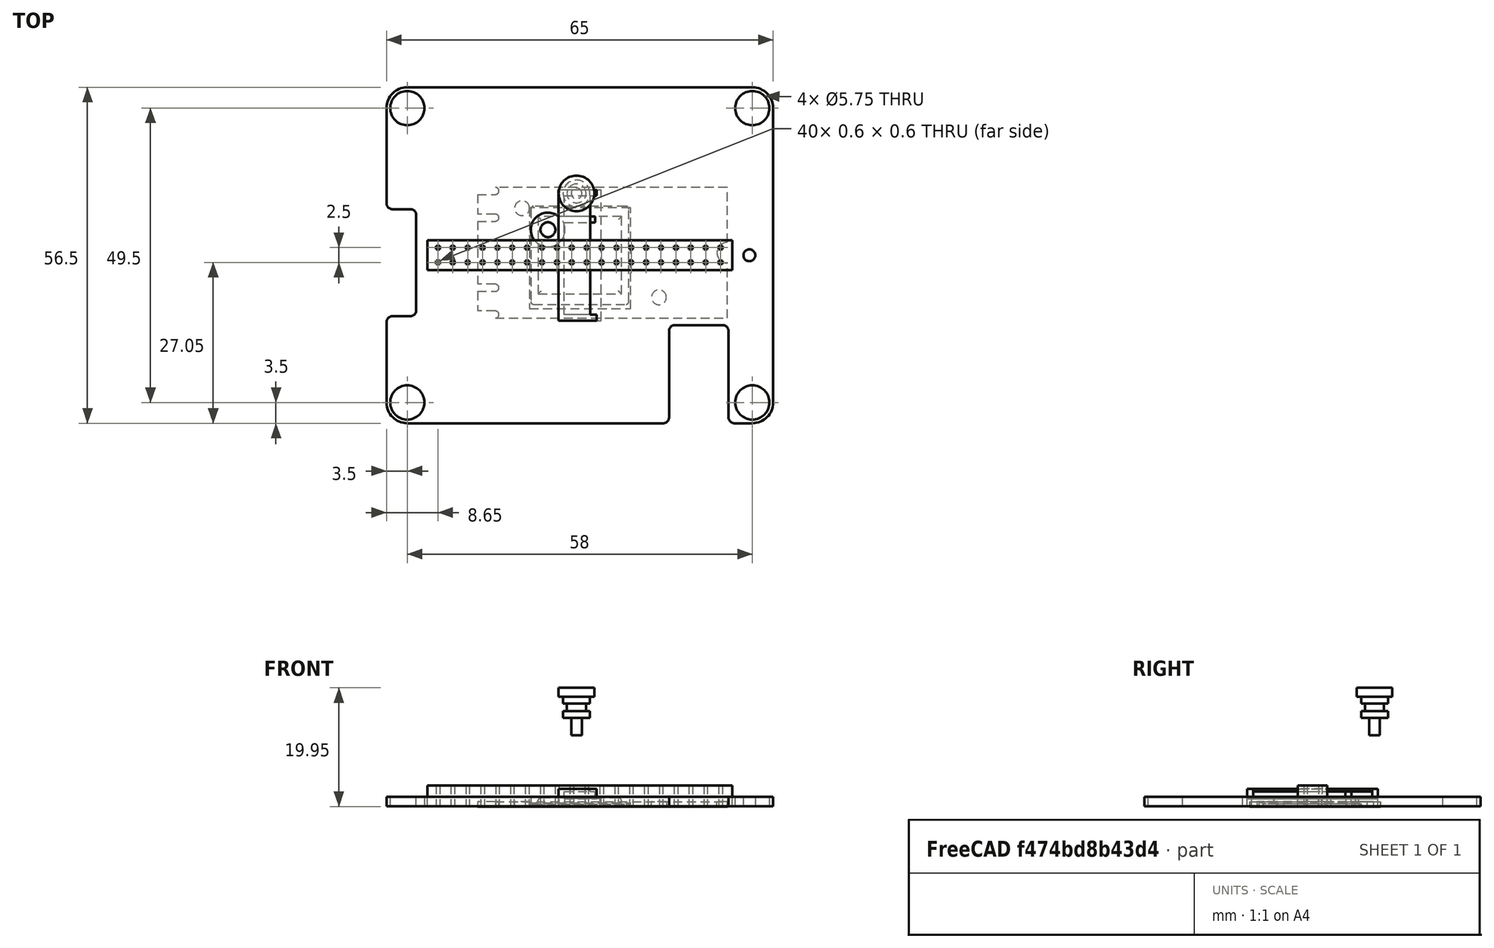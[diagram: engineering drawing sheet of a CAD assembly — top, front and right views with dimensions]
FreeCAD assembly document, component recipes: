
FREECAD ASSEMBLY — COMPONENT RECIPES ("Raspberry Pi AI Kit")

This assembly document has 11 components, labeled P0..P10 below (a component is one placed body or linked part). 11 of them carry a construction recipe — the FreeCAD feature program that regenerates the part from scratch, quoted from this document or its linked companion documents; the rest are supplied as boundary geometry only. No exploded tour is included for this assembly.
COMPONENT P0 — recipe-attached ("Board001", modeled in this document).
Construction recipe (the document's own serialized feature program — sketch geometry with constraints, then the solid features built on it; lengths are millimeters unless a unit is written):

FEATURE [Sketcher::SketchObject] Sketch
  ArcFitTolerance = 1e-06
  AttachmentSupport = -> [XY_Plane003]
  FullyConstrained = true
  MakeInternals = false
  MapMode = 5
  sketch-geometry (6):
    g0: LineSegment StartX=-21 StartY=11 StartZ=0 EndX=-21 EndY=-11 EndZ=0
    g1: LineSegment StartX=-21 StartY=-11 StartZ=0 EndX=21 EndY=-11 EndZ=0
    g2: LineSegment StartX=21 StartY=-11 StartZ=0 EndX=21 EndY=11 EndZ=0
    g3: LineSegment StartX=21 StartY=11 StartZ=0 EndX=-21 EndY=11 EndZ=0
    g4: GeomPoint X=0 Y=11 Z=0
    g5: GeomPoint X=-21 Y=0 Z=0
  constraints (14):
    c: Coincident(g0,g1)
    c: Coincident(g1,g2)
    c: Coincident(g2,g3)
    c: Coincident(g3,g0)
    c: Vertical(g0)
    c: Vertical(g2)
    c: Horizontal(g1)
    c: Horizontal(g3)
    c: DistanceY(g2,g2) = 22
    c: DistanceX(g3,g3) = 42
    c: Symmetric(g3,g3,g4)
    c: Symmetric(g0,g0,g5)
    c: Vertical(g4,g-1)
    c: Horizontal(g5,g-1)
FEATURE [PartDesign::Pad] Pad
  Direction = (0,0,1)
  Length = 0.8
  Length2 = 10
  Profile = -> Sketch
  ReferenceAxis = -> Sketch [N_Axis]
  Refine = true
  Suppressed = false
  Type = 0
FEATURE [Sketcher::SketchObject] Sketch001
  ArcFitTolerance = 1e-06
  AttachmentSupport = -> [Pad]
  ExternalGeometry = -> [Pad]
  FullyConstrained = true
  MakeInternals = false
  MapMode = 5
  Placement = pos=(0,0,0.8) rot=(0,0,1;0rad)
  sketch-geometry (27):
    g0: LineSegment StartX=-21 StartY=-9.8 StartZ=0 EndX=-21 EndY=-11 EndZ=0
    g1: LineSegment StartX=-21 StartY=-11 StartZ=0 EndX=-18 EndY=-11 EndZ=0
    g2: LineSegment StartX=-18 StartY=-11 StartZ=0 EndX=-18 EndY=-9.8 EndZ=0
    g3: LineSegment StartX=-18 StartY=-9.8 StartZ=0 EndX=-21 EndY=-9.8 EndZ=0
    g4: GeomPoint X=-18 Y=-10.4 Z=0
    g5: Circle CenterX=-18 CenterY=-10.4 CenterZ=0 NormalX=0 NormalY=0 NormalZ=1 AngleXU=0 Radius=0.6
    g6: Circle CenterX=21 CenterY=0 CenterZ=0 NormalX=0 NormalY=0 NormalZ=1 AngleXU=0 Radius=1.75
    g7: LineSegment StartX=-21 StartY=11 StartZ=0 EndX=-21 EndY=9.8 EndZ=0
    g8: LineSegment StartX=-21 StartY=9.8 StartZ=0 EndX=-18 EndY=9.8 EndZ=0
    g9: LineSegment StartX=-18 StartY=9.8 StartZ=0 EndX=-18 EndY=11 EndZ=0
    g10: LineSegment StartX=-18 StartY=11 StartZ=0 EndX=-21 EndY=11 EndZ=0
    g11: GeomPoint X=-18 Y=10.4 Z=0
    g12: Circle CenterX=-18 CenterY=10.4 CenterZ=0 NormalX=0 NormalY=0 NormalZ=1 AngleXU=0 Radius=0.6
    g13: LineSegment StartX=-21 StartY=6.5 StartZ=0 EndX=-21 EndY=5.3 EndZ=0
    g14: LineSegment StartX=-21 StartY=5.3 StartZ=0 EndX=-18 EndY=5.3 EndZ=0
    g15: LineSegment StartX=-18 StartY=5.3 StartZ=0 EndX=-18 EndY=6.5 EndZ=0
    g16: LineSegment StartX=-18 StartY=6.5 StartZ=0 EndX=-21 EndY=6.5 EndZ=0
    g17: GeomPoint X=-18 Y=5.9 Z=0
    g18: Circle CenterX=-18 CenterY=5.9 CenterZ=0 NormalX=0 NormalY=0 NormalZ=1 AngleXU=0 Radius=0.6
    g19: LineSegment StartX=-21 StartY=-5.3 StartZ=0 EndX=-21 EndY=-6.5 EndZ=0
    g20: LineSegment StartX=-21 StartY=-6.5 StartZ=0 EndX=-18 EndY=-6.5 EndZ=0
    g21: LineSegment StartX=-18 StartY=-6.5 StartZ=0 EndX=-18 EndY=-5.3 EndZ=0
    g22: LineSegment StartX=-18 StartY=-5.3 StartZ=0 EndX=-21 EndY=-5.3 EndZ=0
    g23: GeomPoint X=-18 Y=-5.9 Z=0
    g24: Circle CenterX=-18 CenterY=-5.9 CenterZ=0 NormalX=0 NormalY=0 NormalZ=1 AngleXU=0 Radius=0.6
    g25: Circle CenterX=-13.5 CenterY=7.5 CenterZ=0 NormalX=0 NormalY=0 NormalZ=1 AngleXU=0 Radius=1.25
    g26: Circle CenterX=9.5 CenterY=-7.5 CenterZ=0 NormalX=0 NormalY=0 NormalZ=1 AngleXU=0 Radius=1.25
  constraints (66):
    c: Coincident(g0,g1)
    c: Coincident(g1,g2)
    c: Coincident(g2,g3)
    c: Coincident(g3,g0)
    c: Vertical(g0)
    c: Vertical(g2)
    c: Horizontal(g1)
    c: Horizontal(g3)
    c: Symmetric(g2,g2,g4)
    c: Coincident(g5,g4)
    c: PointOnObject(g2,g5)
    c: Distance(g1,g3) = 1.2
    c: DistanceX(g3,g3) = 3
    c: Symmetric(g-6,g-6,g6)
    c: Diameter(g6) = 3.5
    c: Coincident(g7,g8)
    c: Coincident(g8,g9)
    c: Coincident(g9,g10)
    c: Coincident(g10,g7)
    c: Vertical(g7)
    c: Vertical(g9)
    c: Horizontal(g8)
    c: Horizontal(g10)
    c: Symmetric(g9,g9,g11)
    c: Coincident(g12,g11)
    c: PointOnObject(g9,g12)
    c: Distance(g8,g10) = 1.2
    c: DistanceX(g10,g10) = 3
    c: Coincident(g0,g-5)
    c: Coincident(g13,g14)
    c: Coincident(g14,g15)
    c: Coincident(g15,g16)
    c: Coincident(g16,g13)
    c: Vertical(g13)
    c: Vertical(g15)
    c: Horizontal(g14)
    c: Horizontal(g16)
    c: Symmetric(g15,g15,g17)
    c: Coincident(g18,g17)
    c: PointOnObject(g15,g18)
    c: Distance(g14,g16) = 1.2
    c: DistanceX(g16,g16) = 3
    c: Coincident(g19,g20)
    c: Coincident(g20,g21)
    c: Coincident(g21,g22)
    c: Coincident(g22,g19)
    c: Vertical(g19)
    c: Vertical(g21)
    c: Horizontal(g20)
    c: Horizontal(g22)
    c: Symmetric(g21,g21,g23)
    c: Coincident(g24,g23)
    c: PointOnObject(g21,g24)
    c: Distance(g20,g22) = 1.2
    c: DistanceX(g22,g22) = 3
    c: Coincident(g7,g-4)
    c: Distance(g-4,g16) = 4.5
    c: PointOnObject(g13,g-3)
    c: Distance(g-5,g20) = 4.5
    c: PointOnObject(g19,g-3)
    c: Diameter(g25) = 2.5
    c: Diameter(g26) = 2.5
    c: Distance(g25,g-5) = 18.5
    c: Distance(g25,g-3) = 7.5
    c: Distance(g26,g-5) = 3.5
    c: Distance(g26,g-3) = 30.5
FEATURE [PartDesign::Pocket] Pocket
  BaseFeature = -> Pad
  Direction = (0,0,-1)
  Length = 5
  Length2 = 5
  Profile = -> Sketch001
  ReferenceAxis = -> Sketch001 [N_Axis]
  Refine = true
  Suppressed = false
  Type = 0
FEATURE [PartDesign::Body] Body  label="Board"
  AllowCompound = false
  Group = -> [Sketch,Pad,Sketch001,Pocket]
  Origin = -> Origin003
  Placement = pos=(3.79899,0.428775,-0.0438795) rot=(0,0,1;0rad)
  Tip = -> Pocket
COMPONENT P1 — recipe-attached ("Board003", modeled in this document).
Construction recipe (the document's own serialized feature program — sketch geometry with constraints, then the solid features built on it; lengths are millimeters unless a unit is written):

FEATURE [Sketcher::SketchObject] Sketch006
  ArcFitTolerance = 1e-06
  AttachmentSupport = -> [XY_Plane010]
  FullyConstrained = true
  MakeInternals = false
  MapMode = 5
  sketch-geometry (38):
    g0: LineSegment StartX=-29 StartY=28.25 StartZ=0 EndX=29 EndY=28.25 EndZ=0
    g1: LineSegment StartX=32.5 StartY=24.75 StartZ=0 EndX=32.5 EndY=-24.75 EndZ=0
    g2: LineSegment StartX=29 StartY=-28.25 StartZ=0 EndX=26 EndY=-28.25 EndZ=0
    g3: LineSegment StartX=25 StartY=-27.25 StartZ=0 EndX=25 EndY=-12.75 EndZ=0
    g4: LineSegment StartX=24 StartY=-11.75 StartZ=0 EndX=16 EndY=-11.75 EndZ=0
    g5: LineSegment StartX=15 StartY=-12.75 StartZ=0 EndX=15 EndY=-27.25 EndZ=0
    g6: LineSegment StartX=14 StartY=-28.25 StartZ=0 EndX=-29 EndY=-28.25 EndZ=0
    g7: GeomPoint X=0 Y=28.25 Z=0
    g8: LineSegment StartX=-32.5 StartY=-24.75 StartZ=0 EndX=-32.5 EndY=-11.25 EndZ=0
    g9: LineSegment StartX=-31.5 StartY=-10.25 StartZ=0 EndX=-28.5 EndY=-10.25 EndZ=0
    g10: LineSegment StartX=-27.5 StartY=-9.25 StartZ=0 EndX=-27.5 EndY=6.75 EndZ=0
    g11: LineSegment StartX=-28.5 StartY=7.75 StartZ=0 EndX=-31.5 EndY=7.75 EndZ=0
    g12: LineSegment StartX=-32.5 StartY=8.75 StartZ=0 EndX=-32.5 EndY=24.75 EndZ=0
    g13: GeomPoint X=32.5 Y=0 Z=0
    g14: ArcOfCircle CenterX=29 CenterY=24.75 CenterZ=0 NormalX=0 NormalY=0 NormalZ=1 AngleXU=0 Radius=3.5 StartAngle=0 EndAngle=1.5708
    g15: GeomPoint [constr] X=32.5 Y=28.25 Z=0
    g16: ArcOfCircle CenterX=-29 CenterY=24.75 CenterZ=0 NormalX=0 NormalY=0 NormalZ=1 AngleXU=0 Radius=3.5 StartAngle=1.5708 EndAngle=3.14159
    g17: GeomPoint [constr] X=-32.5 Y=28.25 Z=0
    g18: ArcOfCircle CenterX=-29 CenterY=-24.75 CenterZ=0 NormalX=0 NormalY=0 NormalZ=1 AngleXU=0 Radius=3.5 StartAngle=3.14159 EndAngle=4.71239
    g19: GeomPoint [constr] X=-32.5 Y=-28.25 Z=0
    g20: ArcOfCircle CenterX=29 CenterY=-24.75 CenterZ=0 NormalX=0 NormalY=0 NormalZ=1 AngleXU=0 Radius=3.5 StartAngle=4.71239 EndAngle=6.28319
    g21: GeomPoint [constr] X=32.5 Y=-28.25 Z=0
    g22: ArcOfCircle CenterX=-31.5 CenterY=8.75 CenterZ=0 NormalX=0 NormalY=0 NormalZ=1 AngleXU=0 Radius=1 StartAngle=3.14159 EndAngle=4.71239
    g23: GeomPoint [constr] X=-32.5 Y=7.75 Z=0
    g24: ArcOfCircle CenterX=-28.5 CenterY=6.75 CenterZ=0 NormalX=0 NormalY=0 NormalZ=1 AngleXU=0 Radius=1 StartAngle=0 EndAngle=1.5708
    g25: GeomPoint [constr] X=-27.5 Y=7.75 Z=0
    g26: ArcOfCircle CenterX=-28.5 CenterY=-9.25 CenterZ=0 NormalX=0 NormalY=0 NormalZ=1 AngleXU=0 Radius=1 StartAngle=4.71239 EndAngle=6.28319
    g27: GeomPoint [constr] X=-27.5 Y=-10.25 Z=0
    g28: ArcOfCircle CenterX=-31.5 CenterY=-11.25 CenterZ=0 NormalX=0 NormalY=0 NormalZ=1 AngleXU=0 Radius=1 StartAngle=1.5708 EndAngle=3.14159
    g29: GeomPoint [constr] X=-32.5 Y=-10.25 Z=0
    g30: ArcOfCircle CenterX=14 CenterY=-27.25 CenterZ=0 NormalX=0 NormalY=0 NormalZ=1 AngleXU=0 Radius=1 StartAngle=4.71239 EndAngle=6.28319
    g31: GeomPoint [constr] X=15 Y=-28.25 Z=0
    g32: ArcOfCircle CenterX=16 CenterY=-12.75 CenterZ=0 NormalX=0 NormalY=0 NormalZ=1 AngleXU=0 Radius=1 StartAngle=1.5708 EndAngle=3.14159
    g33: GeomPoint [constr] X=15 Y=-11.75 Z=0
    g34: ArcOfCircle CenterX=24 CenterY=-12.75 CenterZ=0 NormalX=0 NormalY=0 NormalZ=1 AngleXU=0 Radius=1 StartAngle=4e-16 EndAngle=1.5708
    g35: GeomPoint [constr] X=25 Y=-11.75 Z=0
    g36: ArcOfCircle CenterX=26 CenterY=-27.25 CenterZ=0 NormalX=0 NormalY=0 NormalZ=1 AngleXU=0 Radius=1 StartAngle=3.14159 EndAngle=4.71239
    g37: GeomPoint [constr] X=25 Y=-28.25 Z=0
  constraints (86):
    c: Horizontal(g0)
    c: Vertical(g1)
    c: Horizontal(g2)
    c: Vertical(g3)
    c: Horizontal(g4)
    c: Vertical(g5)
    c: Horizontal(g6)
    c: DistanceX(g17,g15) = 65
    c: Symmetric(g17,g15,g7)
    c: Vertical(g7,g-1)
    c: Horizontal(g37,g31)
    c: DistanceX(g37,g21) = 7.5
    c: DistanceX(g33,g35) = 10
    c: DistanceY(g37,g35) = 16.5
    c: Vertical(g8)
    c: Horizontal(g9)
    c: Vertical(g10)
    c: Horizontal(g11)
    c: Vertical(g12)
    c: Vertical(g23,g29)
    c: Symmetric(g15,g21,g13)
    c: Horizontal(g13,g-1)
    c: DistanceY(g21,g15) = 56.5
    c: DistanceX(g23,g25) = 5
    c: DistanceY(g27,g25) = 18
    c: DistanceY(g19,g29) = 18
    c: PointOnObject(g15,g0)
    c: PointOnObject(g15,g1)
    c: Tangent(g0,g14) = 1.5708
    c: Tangent(g1,g14) = 1.5708
    c: PointOnObject(g17,g0)
    c: PointOnObject(g17,g12)
    c: Tangent(g0,g16) = 1.5708
    c: Tangent(g12,g16) = 1.5708
    c: PointOnObject(g19,g6)
    c: PointOnObject(g19,g8)
    c: Tangent(g6,g18) = 1.5708
    c: Tangent(g8,g18) = 1.5708
    c: PointOnObject(g21,g1)
    c: PointOnObject(g21,g2)
    c: Tangent(g1,g20) = 1.5708
    c: Tangent(g2,g20) = 1.5708
    c: Radius(g20) = 3.5
    c: Radius(g14) = 3.5
    c: Radius(g16) = 3.5
    c: Radius(g18) = 3.5
    c: PointOnObject(g23,g11)
    c: PointOnObject(g23,g12)
    c: Tangent(g11,g22) = 1.5708
    c: Tangent(g12,g22) = 1.5708
    c: PointOnObject(g25,g10)
    c: PointOnObject(g25,g11)
    c: Tangent(g10,g24) = -1.5708
    c: Tangent(g11,g24) = -1.5708
    c: PointOnObject(g27,g9)
    c: PointOnObject(g27,g10)
    c: Tangent(g9,g26) = -1.5708
    c: Tangent(g10,g26) = -1.5708
    c: PointOnObject(g29,g8)
    c: PointOnObject(g29,g9)
    c: Tangent(g8,g28) = 1.5708
    c: Tangent(g9,g28) = 1.5708
    c: PointOnObject(g31,g5)
    c: PointOnObject(g31,g6)
    c: Tangent(g5,g30) = 1.5708
    c: Tangent(g6,g30) = 1.5708
    c: PointOnObject(g33,g4)
    c: PointOnObject(g33,g5)
    c: Tangent(g4,g32) = -1.5708
    c: Tangent(g5,g32) = -1.5708
    c: PointOnObject(g35,g3)
    c: PointOnObject(g35,g4)
    c: Tangent(g3,g34) = -1.5708
    c: Tangent(g4,g34) = -1.5708
    c: PointOnObject(g37,g2)
    c: PointOnObject(g37,g3)
    c: Tangent(g2,g36) = 1.5708
    c: Tangent(g3,g36) = 1.5708
    c: Radius(g22) = 1
    c: Radius(g24) = 1
    c: Radius(g26) = 1
    c: Radius(g28) = 1
    c: Radius(g30) = 1
    c: Radius(g32) = 1
    c: Radius(g34) = 1
    c: Radius(g36) = 1
FEATURE [PartDesign::Pad] Pad004
  Direction = (0,0,1)
  Length = 1.57
  Length2 = 10
  Profile = -> Sketch006
  ReferenceAxis = -> Sketch006 [N_Axis]
  Refine = true
  Suppressed = false
  Type = 0
FEATURE [Sketcher::SketchObject] Sketch007
  ArcFitTolerance = 1e-06
  AttachmentSupport = -> [Pad004]
  ExternalGeometry = -> [Pad004]
  FullyConstrained = true
  MakeInternals = false
  MapMode = 5
  Placement = pos=(0,0,1.57) rot=(0,0,1;0rad)
  sketch-geometry (5):
    g0: Circle CenterX=-29 CenterY=-24.75 CenterZ=0 NormalX=0 NormalY=0 NormalZ=1 AngleXU=0 Radius=2.875
    g1: Circle CenterX=-29 CenterY=24.75 CenterZ=0 NormalX=0 NormalY=0 NormalZ=1 AngleXU=0 Radius=2.875
    g2: Circle CenterX=29 CenterY=24.75 CenterZ=0 NormalX=0 NormalY=0 NormalZ=1 AngleXU=0 Radius=2.875
    g3: Circle CenterX=29 CenterY=-24.75 CenterZ=0 NormalX=0 NormalY=0 NormalZ=1 AngleXU=0 Radius=2.875
    g4: Circle CenterX=28.5 CenterY=0 CenterZ=0 NormalX=0 NormalY=0 NormalZ=1 AngleXU=0 Radius=1
  constraints (15):
    c: Distance(g0,g-3) = 3.5
    c: Distance(g0,g-7) = 3.5
    c: Diameter(g0) = 5.75
    c: Diameter(g1) = 5.75
    c: Diameter(g2) = 5.75
    c: Diameter(g3) = 5.75
    c: Distance(g1,g-6) = 3.5
    c: Distance(g1,g-5) = 3.5
    c: Distance(g2,g-5) = 3.5
    c: Distance(g2,g-4) = 3.5
    c: Distance(g3,g-4) = 3.5
    c: Distance(g3,g-3) = 3.5
    c: PointOnObject(g4,g-1)
    c: Diameter(g4) = 2
    c: Distance(g4,g-4) = 4
FEATURE [PartDesign::Pocket] Pocket001
  BaseFeature = -> Pad004
  Direction = (0,0,-1)
  Length = 5
  Length2 = 5
  Profile = -> Sketch007
  ReferenceAxis = -> Sketch007 [N_Axis]
  Refine = true
  Suppressed = false
  Type = 0
FEATURE [PartDesign::Body] Body004  label="Board002"
  AllowCompound = false
  Group = -> [Sketch006,Pad004,Sketch007,Pocket001]
  Origin = -> Origin010
  Tip = -> Pocket001
COMPONENT P2 — recipe-attached ("Chip001", modeled in this document).
Construction recipe (the document's own serialized feature program — sketch geometry with constraints, then the solid features built on it; lengths are millimeters unless a unit is written):

FEATURE [Sketcher::SketchObject] Sketch004
  ArcFitTolerance = 1e-06
  AttachmentSupport = -> [XY_Plane008]
  FullyConstrained = true
  MakeInternals = false
  MapMode = 5
  sketch-geometry (14):
    g0: LineSegment StartX=-8.25 StartY=7.75 StartZ=0 EndX=-8.25 EndY=-7.75 EndZ=0
    g1: LineSegment StartX=-7.75 StartY=-8.25 StartZ=0 EndX=7.75 EndY=-8.25 EndZ=0
    g2: LineSegment StartX=8.25 StartY=-7.75 StartZ=0 EndX=8.25 EndY=7.75 EndZ=0
    g3: LineSegment StartX=7.75 StartY=8.25 StartZ=0 EndX=-7.75 EndY=8.25 EndZ=0
    g4: GeomPoint X=8.25 Y=0 Z=0
    g5: GeomPoint X=0 Y=8.25 Z=0
    g6: ArcOfCircle CenterX=7.75 CenterY=7.75 CenterZ=0 NormalX=0 NormalY=0 NormalZ=1 AngleXU=0 Radius=0.5 StartAngle=2e-16 EndAngle=1.5708
    g7: GeomPoint [constr] X=8.25 Y=8.25 Z=0
    g8: ArcOfCircle CenterX=-7.75 CenterY=7.75 CenterZ=0 NormalX=0 NormalY=0 NormalZ=1 AngleXU=0 Radius=0.5 StartAngle=1.5708 EndAngle=3.14159
    g9: GeomPoint [constr] X=-8.25 Y=8.25 Z=0
    g10: ArcOfCircle CenterX=-7.75 CenterY=-7.75 CenterZ=0 NormalX=0 NormalY=0 NormalZ=1 AngleXU=0 Radius=0.5 StartAngle=3.14159 EndAngle=4.71239
    g11: GeomPoint [constr] X=-8.25 Y=-8.25 Z=0
    g12: ArcOfCircle CenterX=7.75 CenterY=-7.75 CenterZ=0 NormalX=0 NormalY=0 NormalZ=1 AngleXU=0 Radius=0.5 StartAngle=4.71239 EndAngle=6.28319
    g13: GeomPoint [constr] X=8.25 Y=-8.25 Z=0
  constraints (30):
    c: Vertical(g0)
    c: Vertical(g2)
    c: Horizontal(g1)
    c: Horizontal(g3)
    c: DistanceX(g9,g7) = 16.5
    c: DistanceY(g13,g7) = 16.5
    c: Symmetric(g13,g7,g4)
    c: Symmetric(g7,g9,g5)
    c: Vertical(g5,g-1)
    c: Horizontal(g4,g-1)
    c: PointOnObject(g7,g2)
    c: PointOnObject(g7,g3)
    c: Tangent(g2,g6) = -1.5708
    c: Tangent(g3,g6) = -1.5708
    c: PointOnObject(g9,g0)
    c: PointOnObject(g9,g3)
    c: Tangent(g0,g8) = -1.5708
    c: Tangent(g3,g8) = -1.5708
    c: PointOnObject(g11,g0)
    c: PointOnObject(g11,g1)
    c: Tangent(g0,g10) = -1.5708
    c: Tangent(g1,g10) = -1.5708
    c: PointOnObject(g13,g1)
    c: PointOnObject(g13,g2)
    c: Tangent(g1,g12) = -1.5708
    c: Tangent(g2,g12) = -1.5708
    c: Radius(g8) = 0.5
    c: Radius(g6) = 0.5
    c: Radius(g12) = 0.5
    c: Radius(g10) = 0.5
FEATURE [PartDesign::Pad] Pad002
  Direction = (0,0,1)
  Length = 0.4
  Length2 = 10
  Profile = -> Sketch004
  ReferenceAxis = -> Sketch004 [N_Axis]
  Refine = true
  Suppressed = false
  Type = 0
FEATURE [Sketcher::SketchObject] Sketch005
  ArcFitTolerance = 1e-06
  AttachmentSupport = -> [Pad002]
  FullyConstrained = true
  MakeInternals = false
  MapMode = 5
  Placement = pos=(0,0,0.4) rot=(0,0,1;0rad)
  sketch-geometry (6):
    g0: LineSegment StartX=-7 StartY=6.5 StartZ=0 EndX=-7 EndY=-6.5 EndZ=0
    g1: LineSegment StartX=-7 StartY=-6.5 StartZ=0 EndX=7 EndY=-6.5 EndZ=0
    g2: LineSegment StartX=7 StartY=-6.5 StartZ=0 EndX=7 EndY=6.5 EndZ=0
    g3: LineSegment StartX=7 StartY=6.5 StartZ=0 EndX=-7 EndY=6.5 EndZ=0
    g4: GeomPoint X=0 Y=6.5 Z=0
    g5: GeomPoint X=7 Y=-1e-16 Z=0
  constraints (14):
    c: Coincident(g0,g1)
    c: Coincident(g1,g2)
    c: Coincident(g2,g3)
    c: Coincident(g3,g0)
    c: Vertical(g0)
    c: Vertical(g2)
    c: Horizontal(g1)
    c: Horizontal(g3)
    c: Symmetric(g3,g3,g4)
    c: Symmetric(g2,g2,g5)
    c: Vertical(g4,g-1)
    c: Horizontal(g5,g-1)
    c: DistanceX(g3,g3) = 14
    c: DistanceY(g2,g2) = 13
FEATURE [PartDesign::Pad] Pad003
  BaseFeature = -> Pad002
  Direction = (0,0,1)
  Length = 1
  Length2 = 10
  Profile = -> Sketch005
  ReferenceAxis = -> Sketch005 [N_Axis]
  Refine = true
  Suppressed = false
  Type = 0
FEATURE [PartDesign::Fillet] Fillet
  Base = -> Pad003 [Face15]
  BaseFeature = -> Pad003
  Radius = 0.5
  Refine = true
  SupportTransform = false
  Suppressed = false
  UseAllEdges = false
FEATURE [PartDesign::Body] Body003  label="Chip"
  AllowCompound = false
  Group = -> [Sketch004,Pad002,Sketch005,Pad003,Fillet]
  Origin = -> Origin008
  Tip = -> Fillet
COMPONENT P3 — recipe-attached ("Chip Platform001", modeled in this document).
Construction recipe (the document's own serialized feature program — sketch geometry with constraints, then the solid features built on it; lengths are millimeters unless a unit is written):

FEATURE [Sketcher::SketchObject] Sketch003
  ArcFitTolerance = 1e-06
  AttachmentSupport = -> [XY_Plane007]
  FullyConstrained = false
  MakeInternals = false
  MapMode = 5
  sketch-geometry (4):
    g0: LineSegment StartX=-8.47777 StartY=8.01213 StartZ=0 EndX=-8.47777 EndY=-8.98787 EndZ=0
    g1: LineSegment StartX=-8.47777 StartY=-8.98787 StartZ=0 EndX=8.52223 EndY=-8.98787 EndZ=0
    g2: LineSegment StartX=8.52223 StartY=-8.98787 StartZ=0 EndX=8.52223 EndY=8.01213 EndZ=0
    g3: LineSegment StartX=8.52223 StartY=8.01213 StartZ=0 EndX=-8.47777 EndY=8.01213 EndZ=0
  constraints (10):
    c: Coincident(g0,g1)
    c: Coincident(g1,g2)
    c: Coincident(g2,g3)
    c: Coincident(g3,g0)
    c: Vertical(g0)
    c: Vertical(g2)
    c: Horizontal(g1)
    c: Horizontal(g3)
    c: DistanceX(g3,g3) = 17
    c: DistanceY(g2,g2) = 17
FEATURE [PartDesign::Pad] Pad001
  Direction = (0,0,1)
  Length = 0.6
  Length2 = 10
  Profile = -> Sketch003
  ReferenceAxis = -> Sketch003 [N_Axis]
  Refine = true
  Suppressed = false
  Type = 0
FEATURE [PartDesign::Body] Body002  label="Chip Platform"
  AllowCompound = false
  Group = -> [Sketch003,Pad001]
  Origin = -> Origin007
  Tip = -> Pad001
COMPONENT P4 — recipe-attached ("Hailo Connector001", modeled in this document).
Construction recipe (the document's own serialized feature program — sketch geometry with constraints, then the solid features built on it; lengths are millimeters unless a unit is written):

FEATURE [Sketcher::SketchObject] Sketch009
  ArcFitTolerance = 1e-06
  AttachmentSupport = -> [XY_Plane012]
  FullyConstrained = true
  MakeInternals = false
  MapMode = 5
  sketch-geometry (6):
    g0: LineSegment StartX=-3.6 StartY=11 StartZ=0 EndX=-3.6 EndY=-11 EndZ=0
    g1: LineSegment StartX=-3.6 StartY=-11 StartZ=0 EndX=3.6 EndY=-11 EndZ=0
    g2: LineSegment StartX=3.6 StartY=-11 StartZ=0 EndX=3.6 EndY=11 EndZ=0
    g3: LineSegment StartX=3.6 StartY=11 StartZ=0 EndX=-3.6 EndY=11 EndZ=0
    g4: GeomPoint X=0 Y=11 Z=0
    g5: GeomPoint X=3.6 Y=0 Z=0
  constraints (14):
    c: Coincident(g0,g1)
    c: Coincident(g1,g2)
    c: Coincident(g2,g3)
    c: Coincident(g3,g0)
    c: Vertical(g0)
    c: Vertical(g2)
    c: Horizontal(g1)
    c: Horizontal(g3)
    c: Symmetric(g3,g3,g4)
    c: Symmetric(g2,g2,g5)
    c: Vertical(g4,g-1)
    c: Horizontal(g5,g-1)
    c: DistanceY(g2,g2) = 22
    c: DistanceX(g3,g3) = 7.2
FEATURE [PartDesign::Pad] Pad006
  Direction = (0,0,1)
  Length = 1.25
  Length2 = 10
  Profile = -> Sketch009
  ReferenceAxis = -> Sketch009 [N_Axis]
  Refine = true
  Suppressed = false
  Type = 0
FEATURE [Sketcher::SketchObject] Sketch010
  ArcFitTolerance = 1e-06
  AttachmentSupport = -> [Pad006]
  ExternalGeometry = -> [Pad006]
  FullyConstrained = true
  MakeInternals = false
  MapMode = 5
  Placement = pos=(0,0,1.25) rot=(0,0,1;0rad)
  sketch-geometry (16):
    g0: LineSegment StartX=-3.6 StartY=11 StartZ=0 EndX=-3.6 EndY=-11 EndZ=0
    g1: LineSegment StartX=-3.6 StartY=-11 StartZ=0 EndX=-2.6 EndY=-11 EndZ=0
    g2: LineSegment StartX=-2.6 StartY=-11 StartZ=0 EndX=-2.6 EndY=11 EndZ=0
    g3: LineSegment StartX=-2.6 StartY=11 StartZ=0 EndX=-3.6 EndY=11 EndZ=0
    g4: LineSegment StartX=-2.6 StartY=11 StartZ=0 EndX=-2.6 EndY=10 EndZ=0
    g5: LineSegment StartX=-2.6 StartY=10 StartZ=0 EndX=2.85 EndY=10 EndZ=0
    g6: LineSegment StartX=2.85 StartY=10 StartZ=0 EndX=2.85 EndY=11 EndZ=0
    g7: LineSegment StartX=2.85 StartY=11 StartZ=0 EndX=-2.6 EndY=11 EndZ=0
    g8: LineSegment StartX=-2.6 StartY=6.5 StartZ=0 EndX=-2.6 EndY=5.5 EndZ=0
    g9: LineSegment StartX=-2.6 StartY=5.5 StartZ=0 EndX=2.6 EndY=5.5 EndZ=0
    g10: LineSegment StartX=2.6 StartY=5.5 StartZ=0 EndX=2.6 EndY=6.5 EndZ=0
    g11: LineSegment StartX=2.6 StartY=6.5 StartZ=0 EndX=-2.6 EndY=6.5 EndZ=0
    g12: LineSegment StartX=-2.6 StartY=-11 StartZ=0 EndX=2.85 EndY=-11 EndZ=0
    g13: LineSegment StartX=2.85 StartY=-11 StartZ=0 EndX=2.85 EndY=-10 EndZ=0
    g14: LineSegment StartX=2.85 StartY=-10 StartZ=0 EndX=-2.6 EndY=-10 EndZ=0
    g15: LineSegment StartX=-2.6 StartY=-10 StartZ=0 EndX=-2.6 EndY=-11 EndZ=0
  constraints (45):
    c: Coincident(g0,g1)
    c: Coincident(g1,g2)
    c: Coincident(g2,g3)
    c: Coincident(g3,g0)
    c: Vertical(g0)
    c: Vertical(g2)
    c: Horizontal(g1)
    c: Horizontal(g3)
    c: Coincident(g0,g-6)
    c: PointOnObject(g1,g-5)
    c: Coincident(g4,g5)
    c: Coincident(g5,g6)
    c: Coincident(g6,g7)
    c: Coincident(g7,g4)
    c: Vertical(g4)
    c: Vertical(g6)
    c: Horizontal(g5)
    c: Horizontal(g7)
    c: Coincident(g4,g2)
    c: Coincident(g8,g9)
    c: Coincident(g9,g10)
    c: Coincident(g10,g11)
    c: Coincident(g11,g8)
    c: Vertical(g8)
    c: Vertical(g10)
    c: Horizontal(g9)
    c: Horizontal(g11)
    c: PointOnObject(g8,g2)
    c: Coincident(g12,g13)
    c: Coincident(g13,g14)
    c: Coincident(g14,g15)
    c: Coincident(g15,g12)
    c: Horizontal(g12)
    c: Horizontal(g14)
    c: Vertical(g13)
    c: Vertical(g15)
    c: Coincident(g12,g1)
    c: Distance(g-4,g13) = 0.75
    c: Distance(g-4,g6) = 0.75
    c: Distance(g-4,g10) = 1
    c: DistanceY(g10,g10) = 1
    c: DistanceY(g6,g6) = 1
    c: DistanceY(g13,g13) = 1
    c: DistanceX(g3,g3) = 1
    c: Distance(g7,g11) = 4.5
FEATURE [PartDesign::Pad] Pad007
  BaseFeature = -> Pad006
  Direction = (0,0,1)
  Length = 1.2
  Length2 = 10
  Profile = -> Sketch010
  ReferenceAxis = -> Sketch010 [N_Axis]
  Refine = true
  Suppressed = false
  Type = 0
FEATURE [Sketcher::SketchObject] Sketch011
  ArcFitTolerance = 1e-06
  AttachmentSupport = -> [Pad007]
  ExternalGeometry = -> [Pad007]
  FullyConstrained = true
  MakeInternals = false
  MapMode = 5
  Placement = pos=(0,0,2.45) rot=(0,0,1;0rad)
  sketch-geometry (12):
    g0: LineSegment StartX=-3.6 StartY=11 StartZ=0 EndX=-3.6 EndY=-11 EndZ=0
    g1: LineSegment StartX=-3.6 StartY=-11 StartZ=0 EndX=1.75 EndY=-11 EndZ=0
    g2: LineSegment StartX=1.75 StartY=-11 StartZ=0 EndX=1.75 EndY=11 EndZ=0
    g3: LineSegment StartX=1.75 StartY=11 StartZ=0 EndX=-3.6 EndY=11 EndZ=0
    g4: LineSegment StartX=1.75 StartY=-11 StartZ=0 EndX=2.85 EndY=-11 EndZ=0
    g5: LineSegment StartX=2.85 StartY=-11 StartZ=0 EndX=2.85 EndY=-10 EndZ=0
    g6: LineSegment StartX=2.85 StartY=-10 StartZ=0 EndX=1.75 EndY=-10 EndZ=0
    g7: LineSegment StartX=1.75 StartY=-10 StartZ=0 EndX=1.75 EndY=-11 EndZ=0
    g8: LineSegment StartX=1.75 StartY=11 StartZ=0 EndX=1.75 EndY=10 EndZ=0
    g9: LineSegment StartX=1.75 StartY=10 StartZ=0 EndX=2.85 EndY=10 EndZ=0
    g10: LineSegment StartX=2.85 StartY=10 StartZ=0 EndX=2.85 EndY=11 EndZ=0
    g11: LineSegment StartX=2.85 StartY=11 StartZ=0 EndX=1.75 EndY=11 EndZ=0
  constraints (31):
    c: Coincident(g0,g1)
    c: Coincident(g1,g2)
    c: Coincident(g2,g3)
    c: Coincident(g3,g0)
    c: Vertical(g0)
    c: Vertical(g2)
    c: Horizontal(g1)
    c: Horizontal(g3)
    c: Coincident(g0,g-4)
    c: PointOnObject(g1,g-5)
    c: DistanceX(g3,g3) = 5.35
    c: Coincident(g4,g5)
    c: Coincident(g5,g6)
    c: Coincident(g6,g7)
    c: Coincident(g7,g4)
    c: Horizontal(g4)
    c: Horizontal(g6)
    c: Vertical(g5)
    c: Vertical(g7)
    c: Coincident(g4,g1)
    c: Coincident(g5,g-9)
    c: Coincident(g8,g9)
    c: Coincident(g9,g10)
    c: Coincident(g10,g11)
    c: Coincident(g11,g8)
    c: Vertical(g8)
    c: Vertical(g10)
    c: Horizontal(g9)
    c: Horizontal(g11)
    c: Coincident(g8,g2)
    c: Coincident(g9,g-7)
FEATURE [PartDesign::Pad] Pad008
  BaseFeature = -> Pad007
  Direction = (0,0,1)
  Length = 0.5
  Length2 = 10
  Profile = -> Sketch011
  ReferenceAxis = -> Sketch011 [N_Axis]
  Refine = true
  Suppressed = false
  Type = 0
FEATURE [PartDesign::Body] Body006  label="Hailo Connector"
  AllowCompound = false
  Group = -> [Sketch009,Pad006,Sketch010,Pad007,Sketch011,Pad008]
  Origin = -> Origin012
  Tip = -> Pad008
COMPONENT P5 — recipe-attached ("Hole Inserts001", modeled in this document).
Construction recipe (the document's own serialized feature program — sketch geometry with constraints, then the solid features built on it; lengths are millimeters unless a unit is written):

FEATURE [Sketcher::SketchObject] Sketch008
  ArcFitTolerance = 1e-06
  AttachmentSupport = -> [XY_Plane011]
  FullyConstrained = false
  MakeInternals = false
  MapMode = 5
  sketch-geometry (2):
    g0: Circle CenterX=-5.35776 CenterY=4.30507 CenterZ=0 NormalX=0 NormalY=0 NormalZ=1 AngleXU=0 Radius=2.875
    g1: Circle CenterX=-5.35776 CenterY=4.30507 CenterZ=0 NormalX=0 NormalY=0 NormalZ=1 AngleXU=0 Radius=1.25
  constraints (3):
    c: Diameter(g0) = 5.75
    c: Coincident(g1,g0)
    c: Diameter(g1) = 2.5
FEATURE [PartDesign::Pad] Pad005
  Direction = (0,0,1)
  Length = 1.57
  Length2 = 10
  Profile = -> Sketch008
  ReferenceAxis = -> Sketch008 [N_Axis]
  Refine = true
  Suppressed = false
  Type = 0
FEATURE [PartDesign::Body] Body005  label="Hole Inserts"
  AllowCompound = false
  Group = -> [Sketch008,Pad005]
  Origin = -> Origin011
  Tip = -> Pad005
COMPONENT P6 — same part as P5; its construction recipe is shown at P5.
COMPONENT P7 — same part as P5; its construction recipe is shown at P5.
COMPONENT P8 — same part as P5; its construction recipe is shown at P5.
COMPONENT P9 — recipe-attached ("Pin001", modeled in this document).
Construction recipe (the document's own serialized feature program — sketch geometry with constraints, then the solid features built on it; lengths are millimeters unless a unit is written):

FEATURE [Sketcher::SketchObject] Sketch002
  ArcFitTolerance = 1e-06
  AttachmentSupport = -> [XZ_Plane004]
  FullyConstrained = false
  MakeInternals = false
  MapMode = 5
  Placement = pos=(0,0,0) rot=(1,0,0;1.5708rad)
  sketch-geometry (20):
    g0: LineSegment StartX=0 StartY=8.4139 StartZ=0 EndX=-0.9 EndY=8.4139 EndZ=0
    g1: LineSegment StartX=-0.9 StartY=8.4139 StartZ=0 EndX=-0.9 EndY=0.413896 EndZ=0
    g2: LineSegment StartX=-0.9 StartY=0.413896 StartZ=0 EndX=0 EndY=0.413896 EndZ=0
    g3: LineSegment StartX=0 StartY=0.413896 StartZ=0 EndX=0 EndY=8.4139 EndZ=0
    g4: LineSegment StartX=-0.9 StartY=8.4139 StartZ=0 EndX=-3 EndY=8.4139 EndZ=0
    g5: LineSegment StartX=-3 StartY=8.4139 StartZ=0 EndX=-3 EndY=6.9139 EndZ=0
    g6: LineSegment StartX=-3 StartY=6.9139 StartZ=0 EndX=-0.9 EndY=6.9139 EndZ=0
    g7: LineSegment StartX=-0.9 StartY=6.9139 StartZ=0 EndX=-0.9 EndY=8.4139 EndZ=0
    g8: LineSegment StartX=-2.25 StartY=6.9139 StartZ=0 EndX=-2.25 EndY=5.7639 EndZ=0
    g9: LineSegment StartX=-2.25 StartY=5.7639 StartZ=0 EndX=-0.9 EndY=5.7639 EndZ=0
    g10: LineSegment StartX=-0.9 StartY=5.7639 StartZ=0 EndX=-0.9 EndY=6.9139 EndZ=0
    g11: LineSegment StartX=-0.9 StartY=6.9139 StartZ=0 EndX=-2.25 EndY=6.9139 EndZ=0
    g12: LineSegment StartX=-0.9 StartY=4.5139 StartZ=0 EndX=-2.25 EndY=4.5139 EndZ=0
    g13: LineSegment StartX=-2.25 StartY=4.5139 StartZ=0 EndX=-2.25 EndY=3.3639 EndZ=0
    g14: LineSegment StartX=-2.25 StartY=3.3639 StartZ=0 EndX=-0.9 EndY=3.3639 EndZ=0
    g15: LineSegment StartX=-0.9 StartY=3.3639 StartZ=0 EndX=-0.9 EndY=4.5139 EndZ=0
    g16: LineSegment StartX=-1.6 StartY=5.7639 StartZ=0 EndX=-1.6 EndY=4.5139 EndZ=0
    g17: LineSegment StartX=-1.6 StartY=4.5139 StartZ=0 EndX=-0.9 EndY=4.5139 EndZ=0
    g18: LineSegment StartX=-0.9 StartY=4.5139 StartZ=0 EndX=-0.9 EndY=5.7639 EndZ=0
    g19: LineSegment StartX=-0.9 StartY=5.7639 StartZ=0 EndX=-1.6 EndY=5.7639 EndZ=0
  constraints (57):
    c: Coincident(g0,g1)
    c: Coincident(g1,g2)
    c: Coincident(g2,g3)
    c: Coincident(g3,g0)
    c: Horizontal(g0)
    c: Horizontal(g2)
    c: Vertical(g1)
    c: Vertical(g3)
    c: PointOnObject(g0,g-2)
    c: DistanceX(g0,g0) = 0.9
    c: Coincident(g4,g5)
    c: Coincident(g5,g6)
    c: Coincident(g6,g7)
    c: Coincident(g7,g4)
    c: Horizontal(g4)
    c: Horizontal(g6)
    c: Vertical(g5)
    c: Vertical(g7)
    c: Coincident(g4,g0)
    c: DistanceY(g3,g3) = 8
    c: Distance(g6,g4) = 1.5
    c: DistanceX(g4,g0) = 3
    c: Coincident(g8,g9)
    c: Coincident(g9,g10)
    c: Coincident(g10,g11)
    c: Coincident(g11,g8)
    c: Vertical(g8)
    c: Vertical(g10)
    c: Horizontal(g9)
    c: Horizontal(g11)
    c: PointOnObject(g8,g6)
    c: PointOnObject(g9,g1)
    c: Distance(g8,g3) = 2.25
    c: DistanceY(g8,g8) = 1.15
    c: Coincident(g12,g13)
    c: Coincident(g13,g14)
    c: Coincident(g14,g15)
    c: Coincident(g15,g12)
    c: Horizontal(g12)
    c: Horizontal(g14)
    c: Vertical(g13)
    c: Vertical(g15)
    c: PointOnObject(g12,g1)
    c: DistanceY(g13,g13) = 1.15
    c: Distance(g12,g9) = 1.25
    c: Vertical(g8,g12)
    c: Coincident(g16,g17)
    c: Coincident(g17,g18)
    c: Coincident(g18,g19)
    c: Coincident(g19,g16)
    c: Vertical(g16)
    c: Vertical(g18)
    c: Horizontal(g17)
    c: Horizontal(g19)
    c: PointOnObject(g16,g9)
    c: Coincident(g17,g12)
    c: Distance(g3,g16) = 1.6
FEATURE [PartDesign::Revolution] Revolution
  Angle = 360
  Angle2 = 60
  Axis = (0,2e-16,1)
  Base = (0,0,0)
  Placement = pos=(0,0,0) rot=(1,0,0;1.5708rad)
  Profile = -> Sketch002
  ReferenceAxis = -> Sketch002 [V_Axis]
  Refine = true
  Suppressed = false
  Type = 0
FEATURE [PartDesign::Body] Body001  label="Pin"
  AllowCompound = false
  Group = -> [Sketch002,Revolution]
  Origin = -> Origin004
  Placement = pos=(-0.558638,10.4085,11.496) rot=(0,0,1;0rad)
  Tip = -> Revolution
COMPONENT P10 — recipe-attached ("Pin Block001", modeled in this document).
Construction recipe (the document's own serialized feature program — sketch geometry with constraints, then the solid features built on it; lengths are millimeters unless a unit is written):

FEATURE [Sketcher::SketchObject] Sketch012
  ArcFitTolerance = 1e-06
  AttachmentSupport = -> [XY_Plane013]
  FullyConstrained = true
  MakeInternals = false
  MapMode = 5
  sketch-geometry (6):
    g0: LineSegment StartX=-25.65 StartY=2.5 StartZ=0 EndX=-25.65 EndY=-2.5 EndZ=0
    g1: LineSegment StartX=-25.65 StartY=-2.5 StartZ=0 EndX=25.65 EndY=-2.5 EndZ=0
    g2: LineSegment StartX=25.65 StartY=-2.5 StartZ=0 EndX=25.65 EndY=2.5 EndZ=0
    g3: LineSegment StartX=25.65 StartY=2.5 StartZ=0 EndX=-25.65 EndY=2.5 EndZ=0
    g4: GeomPoint X=0 Y=2.5 Z=0
    g5: GeomPoint X=-25.65 Y=0 Z=0
  constraints (14):
    c: Coincident(g0,g1)
    c: Coincident(g1,g2)
    c: Coincident(g2,g3)
    c: Coincident(g3,g0)
    c: Vertical(g0)
    c: Vertical(g2)
    c: Horizontal(g1)
    c: Horizontal(g3)
    c: DistanceX(g3,g3) = 51.3
    c: DistanceY(g0,g0) = 5
    c: Symmetric(g3,g3,g4)
    c: Symmetric(g0,g0,g5)
    c: Vertical(g4,g-1)
    c: Horizontal(g-1,g5)
FEATURE [PartDesign::Pad] Pad009
  Direction = (0,0,1)
  Length = 3.5
  Length2 = 10
  Profile = -> Sketch012
  ReferenceAxis = -> Sketch012 [N_Axis]
  Refine = true
  Suppressed = false
  Type = 0
FEATURE [Sketcher::SketchObject] Sketch013
  ArcFitTolerance = 1e-06
  AttachmentSupport = -> [Pad009]
  ExternalGeometry = -> [Pad009]
  FullyConstrained = true
  MakeInternals = false
  MapMode = 5
  Placement = pos=(0,0,3.5) rot=(0,0,1;0rad)
  sketch-geometry (160):
    g0: LineSegment StartX=13.35 StartY=-0.9 StartZ=0 EndX=13.35 EndY=-1.5 EndZ=0
    g1: LineSegment StartX=13.35 StartY=-1.5 StartZ=0 EndX=13.95 EndY=-1.5 EndZ=0
    g2: LineSegment StartX=13.95 StartY=-1.5 StartZ=0 EndX=13.95 EndY=-0.9 EndZ=0
    g3: LineSegment StartX=13.95 StartY=-0.9 StartZ=0 EndX=13.35 EndY=-0.9 EndZ=0
    g4: LineSegment StartX=13.35 StartY=1.6 StartZ=0 EndX=13.35 EndY=1 EndZ=0
    g5: LineSegment StartX=13.35 StartY=1 StartZ=0 EndX=13.95 EndY=1 EndZ=0
    g6: LineSegment StartX=13.95 StartY=1 StartZ=0 EndX=13.95 EndY=1.6 EndZ=0
    g7: LineSegment StartX=13.95 StartY=1.6 StartZ=0 EndX=13.35 EndY=1.6 EndZ=0
    g8: LineSegment StartX=10.85 StartY=-0.9 StartZ=0 EndX=10.85 EndY=-1.5 EndZ=0
    g9: LineSegment StartX=10.85 StartY=-1.5 StartZ=0 EndX=11.45 EndY=-1.5 EndZ=0
    g10: LineSegment StartX=11.45 StartY=-1.5 StartZ=0 EndX=11.45 EndY=-0.9 EndZ=0
    g11: LineSegment StartX=11.45 StartY=-0.9 StartZ=0 EndX=10.85 EndY=-0.9 EndZ=0
    g12: LineSegment StartX=10.85 StartY=1.6 StartZ=0 EndX=10.85 EndY=1 EndZ=0
    g13: LineSegment StartX=10.85 StartY=1 StartZ=0 EndX=11.45 EndY=1 EndZ=0
    g14: LineSegment StartX=11.45 StartY=1 StartZ=0 EndX=11.45 EndY=1.6 EndZ=0
    g15: LineSegment StartX=11.45 StartY=1.6 StartZ=0 EndX=10.85 EndY=1.6 EndZ=0
    g16: LineSegment StartX=8.35 StartY=-0.9 StartZ=0 EndX=8.35 EndY=-1.5 EndZ=0
    g17: LineSegment StartX=8.35 StartY=-1.5 StartZ=0 EndX=8.95 EndY=-1.5 EndZ=0
    g18: LineSegment StartX=8.95 StartY=-1.5 StartZ=0 EndX=8.95 EndY=-0.9 EndZ=0
    g19: LineSegment StartX=8.95 StartY=-0.9 StartZ=0 EndX=8.35 EndY=-0.9 EndZ=0
    g20: LineSegment StartX=8.35 StartY=1.6 StartZ=0 EndX=8.35 EndY=1 EndZ=0
    g21: LineSegment StartX=8.35 StartY=1 StartZ=0 EndX=8.95 EndY=1 EndZ=0
    g22: LineSegment StartX=8.95 StartY=1 StartZ=0 EndX=8.95 EndY=1.6 EndZ=0
    g23: LineSegment StartX=8.95 StartY=1.6 StartZ=0 EndX=8.35 EndY=1.6 EndZ=0
    g24: LineSegment StartX=5.85 StartY=-0.9 StartZ=0 EndX=5.85 EndY=-1.5 EndZ=0
    g25: LineSegment StartX=5.85 StartY=-1.5 StartZ=0 EndX=6.45 EndY=-1.5 EndZ=0
    g26: LineSegment StartX=6.45 StartY=-1.5 StartZ=0 EndX=6.45 EndY=-0.9 EndZ=0
    g27: LineSegment StartX=6.45 StartY=-0.9 StartZ=0 EndX=5.85 EndY=-0.9 EndZ=0
    g28: LineSegment StartX=5.85 StartY=1.6 StartZ=0 EndX=5.85 EndY=1 EndZ=0
    g29: LineSegment StartX=5.85 StartY=1 StartZ=0 EndX=6.45 EndY=1 EndZ=0
    g30: LineSegment StartX=6.45 StartY=1 StartZ=0 EndX=6.45 EndY=1.6 EndZ=0
    g31: LineSegment StartX=6.45 StartY=1.6 StartZ=0 EndX=5.85 EndY=1.6 EndZ=0
    g32: LineSegment StartX=3.35 StartY=-0.9 StartZ=0 EndX=3.35 EndY=-1.5 EndZ=0
    g33: LineSegment StartX=3.35 StartY=-1.5 StartZ=0 EndX=3.95 EndY=-1.5 EndZ=0
    g34: LineSegment StartX=3.95 StartY=-1.5 StartZ=0 EndX=3.95 EndY=-0.9 EndZ=0
    g35: LineSegment StartX=3.95 StartY=-0.9 StartZ=0 EndX=3.35 EndY=-0.9 EndZ=0
    g36: LineSegment StartX=3.35 StartY=1.6 StartZ=0 EndX=3.35 EndY=1 EndZ=0
    g37: LineSegment StartX=3.35 StartY=1 StartZ=0 EndX=3.95 EndY=1 EndZ=0
    g38: LineSegment StartX=3.95 StartY=1 StartZ=0 EndX=3.95 EndY=1.6 EndZ=0
    g39: LineSegment StartX=3.95 StartY=1.6 StartZ=0 EndX=3.35 EndY=1.6 EndZ=0
    g40: LineSegment StartX=0.85 StartY=-0.9 StartZ=0 EndX=0.85 EndY=-1.5 EndZ=0
    g41: LineSegment StartX=0.85 StartY=-1.5 StartZ=0 EndX=1.45 EndY=-1.5 EndZ=0
    g42: LineSegment StartX=1.45 StartY=-1.5 StartZ=0 EndX=1.45 EndY=-0.9 EndZ=0
    g43: LineSegment StartX=1.45 StartY=-0.9 StartZ=0 EndX=0.85 EndY=-0.9 EndZ=0
    g44: LineSegment StartX=0.85 StartY=1.6 StartZ=0 EndX=0.85 EndY=1 EndZ=0
    g45: LineSegment StartX=0.85 StartY=1 StartZ=0 EndX=1.45 EndY=1 EndZ=0
    g46: LineSegment StartX=1.45 StartY=1 StartZ=0 EndX=1.45 EndY=1.6 EndZ=0
    g47: LineSegment StartX=1.45 StartY=1.6 StartZ=0 EndX=0.85 EndY=1.6 EndZ=0
    g48: LineSegment StartX=-1.65 StartY=-0.9 StartZ=0 EndX=-1.65 EndY=-1.5 EndZ=0
    g49: LineSegment StartX=-1.65 StartY=-1.5 StartZ=0 EndX=-1.05 EndY=-1.5 EndZ=0
    g50: LineSegment StartX=-1.05 StartY=-1.5 StartZ=0 EndX=-1.05 EndY=-0.9 EndZ=0
    g51: LineSegment StartX=-1.05 StartY=-0.9 StartZ=0 EndX=-1.65 EndY=-0.9 EndZ=0
    g52: LineSegment StartX=-1.65 StartY=1.6 StartZ=0 EndX=-1.65 EndY=1 EndZ=0
    g53: LineSegment StartX=-1.65 StartY=1 StartZ=0 EndX=-1.05 EndY=1 EndZ=0
    g54: LineSegment StartX=-1.05 StartY=1 StartZ=0 EndX=-1.05 EndY=1.6 EndZ=0
    g55: LineSegment StartX=-1.05 StartY=1.6 StartZ=0 EndX=-1.65 EndY=1.6 EndZ=0
    g56: LineSegment StartX=-4.15 StartY=-0.9 StartZ=0 EndX=-4.15 EndY=-1.5 EndZ=0
    g57: LineSegment StartX=-4.15 StartY=-1.5 StartZ=0 EndX=-3.55 EndY=-1.5 EndZ=0
    g58: LineSegment StartX=-3.55 StartY=-1.5 StartZ=0 EndX=-3.55 EndY=-0.9 EndZ=0
    g59: LineSegment StartX=-3.55 StartY=-0.9 StartZ=0 EndX=-4.15 EndY=-0.9 EndZ=0
    g60: LineSegment StartX=-4.15 StartY=1.6 StartZ=0 EndX=-4.15 EndY=1 EndZ=0
    g61: LineSegment StartX=-4.15 StartY=1 StartZ=0 EndX=-3.55 EndY=1 EndZ=0
    g62: LineSegment StartX=-3.55 StartY=1 StartZ=0 EndX=-3.55 EndY=1.6 EndZ=0
    g63: LineSegment StartX=-3.55 StartY=1.6 StartZ=0 EndX=-4.15 EndY=1.6 EndZ=0
    g64: LineSegment StartX=-6.65 StartY=-0.9 StartZ=0 EndX=-6.65 EndY=-1.5 EndZ=0
    g65: LineSegment StartX=-6.65 StartY=-1.5 StartZ=0 EndX=-6.05 EndY=-1.5 EndZ=0
    g66: LineSegment StartX=-6.05 StartY=-1.5 StartZ=0 EndX=-6.05 EndY=-0.9 EndZ=0
    g67: LineSegment StartX=-6.05 StartY=-0.9 StartZ=0 EndX=-6.65 EndY=-0.9 EndZ=0
    g68: LineSegment StartX=-6.65 StartY=1.6 StartZ=0 EndX=-6.65 EndY=1 EndZ=0
    g69: LineSegment StartX=-6.65 StartY=1 StartZ=0 EndX=-6.05 EndY=1 EndZ=0
    g70: LineSegment StartX=-6.05 StartY=1 StartZ=0 EndX=-6.05 EndY=1.6 EndZ=0
    g71: LineSegment StartX=-6.05 StartY=1.6 StartZ=0 EndX=-6.65 EndY=1.6 EndZ=0
    g72: LineSegment StartX=-9.15 StartY=-0.9 StartZ=0 EndX=-9.15 EndY=-1.5 EndZ=0
    g73: LineSegment StartX=-9.15 StartY=-1.5 StartZ=0 EndX=-8.55 EndY=-1.5 EndZ=0
    g74: LineSegment StartX=-8.55 StartY=-1.5 StartZ=0 EndX=-8.55 EndY=-0.9 EndZ=0
    g75: LineSegment StartX=-8.55 StartY=-0.9 StartZ=0 EndX=-9.15 EndY=-0.9 EndZ=0
    g76: LineSegment StartX=-9.15 StartY=1.6 StartZ=0 EndX=-9.15 EndY=1 EndZ=0
    g77: LineSegment StartX=-9.15 StartY=1 StartZ=0 EndX=-8.55 EndY=1 EndZ=0
    g78: LineSegment StartX=-8.55 StartY=1 StartZ=0 EndX=-8.55 EndY=1.6 EndZ=0
    g79: LineSegment StartX=-8.55 StartY=1.6 StartZ=0 EndX=-9.15 EndY=1.6 EndZ=0
    g80: LineSegment StartX=-11.65 StartY=-0.9 StartZ=0 EndX=-11.65 EndY=-1.5 EndZ=0
    g81: LineSegment StartX=-11.65 StartY=-1.5 StartZ=0 EndX=-11.05 EndY=-1.5 EndZ=0
    g82: LineSegment StartX=-11.05 StartY=-1.5 StartZ=0 EndX=-11.05 EndY=-0.9 EndZ=0
    g83: LineSegment StartX=-11.05 StartY=-0.9 StartZ=0 EndX=-11.65 EndY=-0.9 EndZ=0
    g84: LineSegment StartX=-11.65 StartY=1.6 StartZ=0 EndX=-11.65 EndY=1 EndZ=0
    g85: LineSegment StartX=-11.65 StartY=1 StartZ=0 EndX=-11.05 EndY=1 EndZ=0
    g86: LineSegment StartX=-11.05 StartY=1 StartZ=0 EndX=-11.05 EndY=1.6 EndZ=0
    g87: LineSegment StartX=-11.05 StartY=1.6 StartZ=0 EndX=-11.65 EndY=1.6 EndZ=0
    g88: LineSegment StartX=-14.15 StartY=-0.9 StartZ=0 EndX=-14.15 EndY=-1.5 EndZ=0
    g89: LineSegment StartX=-14.15 StartY=-1.5 StartZ=0 EndX=-13.55 EndY=-1.5 EndZ=0
    g90: LineSegment StartX=-13.55 StartY=-1.5 StartZ=0 EndX=-13.55 EndY=-0.9 EndZ=0
    g91: LineSegment StartX=-13.55 StartY=-0.9 StartZ=0 EndX=-14.15 EndY=-0.9 EndZ=0
    g92: LineSegment StartX=-14.15 StartY=1.6 StartZ=0 EndX=-14.15 EndY=1 EndZ=0
    g93: LineSegment StartX=-14.15 StartY=1 StartZ=0 EndX=-13.55 EndY=1 EndZ=0
    g94: LineSegment StartX=-13.55 StartY=1 StartZ=0 EndX=-13.55 EndY=1.6 EndZ=0
    g95: LineSegment StartX=-13.55 StartY=1.6 StartZ=0 EndX=-14.15 EndY=1.6 EndZ=0
    g96: LineSegment StartX=-16.65 StartY=-0.9 StartZ=0 EndX=-16.65 EndY=-1.5 EndZ=0
    g97: LineSegment StartX=-16.65 StartY=-1.5 StartZ=0 EndX=-16.05 EndY=-1.5 EndZ=0
    g98: LineSegment StartX=-16.05 StartY=-1.5 StartZ=0 EndX=-16.05 EndY=-0.9 EndZ=0
    g99: LineSegment StartX=-16.05 StartY=-0.9 StartZ=0 EndX=-16.65 EndY=-0.9 EndZ=0
    g100: LineSegment StartX=-16.65 StartY=1.6 StartZ=0 EndX=-16.65 EndY=1 EndZ=0
    g101: LineSegment StartX=-16.65 StartY=1 StartZ=0 EndX=-16.05 EndY=1 EndZ=0
    g102: LineSegment StartX=-16.05 StartY=1 StartZ=0 EndX=-16.05 EndY=1.6 EndZ=0
    g103: LineSegment StartX=-16.05 StartY=1.6 StartZ=0 EndX=-16.65 EndY=1.6 EndZ=0
    g104: LineSegment StartX=-19.15 StartY=-0.9 StartZ=0 EndX=-19.15 EndY=-1.5 EndZ=0
    g105: LineSegment StartX=-19.15 StartY=-1.5 StartZ=0 EndX=-18.55 EndY=-1.5 EndZ=0
    g106: LineSegment StartX=-18.55 StartY=-1.5 StartZ=0 EndX=-18.55 EndY=-0.9 EndZ=0
    g107: LineSegment StartX=-18.55 StartY=-0.9 StartZ=0 EndX=-19.15 EndY=-0.9 EndZ=0
    g108: LineSegment StartX=-19.15 StartY=1.6 StartZ=0 EndX=-19.15 EndY=1 EndZ=0
    g109: LineSegment StartX=-19.15 StartY=1 StartZ=0 EndX=-18.55 EndY=1 EndZ=0
    g110: LineSegment StartX=-18.55 StartY=1 StartZ=0 EndX=-18.55 EndY=1.6 EndZ=0
    g111: LineSegment StartX=-18.55 StartY=1.6 StartZ=0 EndX=-19.15 EndY=1.6 EndZ=0
    g112: LineSegment StartX=-21.65 StartY=-0.9 StartZ=0 EndX=-21.65 EndY=-1.5 EndZ=0
    g113: LineSegment StartX=-21.65 StartY=-1.5 StartZ=0 EndX=-21.05 EndY=-1.5 EndZ=0
    g114: LineSegment StartX=-21.05 StartY=-1.5 StartZ=0 EndX=-21.05 EndY=-0.9 EndZ=0
    g115: LineSegment StartX=-21.05 StartY=-0.9 StartZ=0 EndX=-21.65 EndY=-0.9 EndZ=0
    g116: LineSegment StartX=-21.65 StartY=1.6 StartZ=0 EndX=-21.65 EndY=1 EndZ=0
    g117: LineSegment StartX=-21.65 StartY=1 StartZ=0 EndX=-21.05 EndY=1 EndZ=0
    g118: LineSegment StartX=-21.05 StartY=1 StartZ=0 EndX=-21.05 EndY=1.6 EndZ=0
    g119: LineSegment StartX=-21.05 StartY=1.6 StartZ=0 EndX=-21.65 EndY=1.6 EndZ=0
    g120: LineSegment StartX=-24.15 StartY=-0.9 StartZ=0 EndX=-24.15 EndY=-1.5 EndZ=0
    g121: LineSegment StartX=-24.15 StartY=-1.5 StartZ=0 EndX=-23.55 EndY=-1.5 EndZ=0
    g122: LineSegment StartX=-23.55 StartY=-1.5 StartZ=0 EndX=-23.55 EndY=-0.9 EndZ=0
    g123: LineSegment StartX=-23.55 StartY=-0.9 StartZ=0 EndX=-24.15 EndY=-0.9 EndZ=0
    g124: LineSegment StartX=-24.15 StartY=1.6 StartZ=0 EndX=-24.15 EndY=1 EndZ=0
    g125: LineSegment StartX=-24.15 StartY=1 StartZ=0 EndX=-23.55 EndY=1 EndZ=0
    g126: LineSegment StartX=-23.55 StartY=1 StartZ=0 EndX=-23.55 EndY=1.6 EndZ=0
    g127: LineSegment StartX=-23.55 StartY=1.6 StartZ=0 EndX=-24.15 EndY=1.6 EndZ=0
    g128: LineSegment StartX=23.35 StartY=-0.9 StartZ=0 EndX=23.35 EndY=-1.5 EndZ=0
    g129: LineSegment StartX=23.35 StartY=-1.5 StartZ=0 EndX=23.95 EndY=-1.5 EndZ=0
    g130: LineSegment StartX=23.95 StartY=-1.5 StartZ=0 EndX=23.95 EndY=-0.9 EndZ=0
    g131: LineSegment StartX=23.95 StartY=-0.9 StartZ=0 EndX=23.35 EndY=-0.9 EndZ=0
    g132: LineSegment StartX=23.35 StartY=1.6 StartZ=0 EndX=23.35 EndY=1 EndZ=0
    g133: LineSegment StartX=23.35 StartY=1 StartZ=0 EndX=23.95 EndY=1 EndZ=0
    g134: LineSegment StartX=23.95 StartY=1 StartZ=0 EndX=23.95 EndY=1.6 EndZ=0
    g135: LineSegment StartX=23.95 StartY=1.6 StartZ=0 EndX=23.35 EndY=1.6 EndZ=0
    g136: LineSegment StartX=20.85 StartY=-0.9 StartZ=0 EndX=20.85 EndY=-1.5 EndZ=0
    g137: LineSegment StartX=20.85 StartY=-1.5 StartZ=0 EndX=21.45 EndY=-1.5 EndZ=0
    g138: LineSegment StartX=21.45 StartY=-1.5 StartZ=0 EndX=21.45 EndY=-0.9 EndZ=0
    g139: LineSegment StartX=21.45 StartY=-0.9 StartZ=0 EndX=20.85 EndY=-0.9 EndZ=0
    g140: LineSegment StartX=20.85 StartY=1.6 StartZ=0 EndX=20.85 EndY=1 EndZ=0
    g141: LineSegment StartX=20.85 StartY=1 StartZ=0 EndX=21.45 EndY=1 EndZ=0
    g142: LineSegment StartX=21.45 StartY=1 StartZ=0 EndX=21.45 EndY=1.6 EndZ=0
    g143: LineSegment StartX=21.45 StartY=1.6 StartZ=0 EndX=20.85 EndY=1.6 EndZ=0
    g144: LineSegment StartX=18.35 StartY=-0.9 StartZ=0 EndX=18.35 EndY=-1.5 EndZ=0
    g145: LineSegment StartX=18.35 StartY=-1.5 StartZ=0 EndX=18.95 EndY=-1.5 EndZ=0
    g146: LineSegment StartX=18.95 StartY=-1.5 StartZ=0 EndX=18.95 EndY=-0.9 EndZ=0
    g147: LineSegment StartX=18.95 StartY=-0.9 StartZ=0 EndX=18.35 EndY=-0.9 EndZ=0
    g148: LineSegment StartX=18.35 StartY=1.6 StartZ=0 EndX=18.35 EndY=1 EndZ=0
    g149: LineSegment StartX=18.35 StartY=1 StartZ=0 EndX=18.95 EndY=1 EndZ=0
    g150: LineSegment StartX=18.95 StartY=1 StartZ=0 EndX=18.95 EndY=1.6 EndZ=0
    g151: LineSegment StartX=18.95 StartY=1.6 StartZ=0 EndX=18.35 EndY=1.6 EndZ=0
    g152: LineSegment StartX=15.85 StartY=-0.9 StartZ=0 EndX=15.85 EndY=-1.5 EndZ=0
    g153: LineSegment StartX=15.85 StartY=-1.5 StartZ=0 EndX=16.45 EndY=-1.5 EndZ=0
    g154: LineSegment StartX=16.45 StartY=-1.5 StartZ=0 EndX=16.45 EndY=-0.9 EndZ=0
    g155: LineSegment StartX=16.45 StartY=-0.9 StartZ=0 EndX=15.85 EndY=-0.9 EndZ=0
    g156: LineSegment StartX=15.85 StartY=1.6 StartZ=0 EndX=15.85 EndY=1 EndZ=0
    g157: LineSegment StartX=15.85 StartY=1 StartZ=0 EndX=16.45 EndY=1 EndZ=0
    g158: LineSegment StartX=16.45 StartY=1 StartZ=0 EndX=16.45 EndY=1.6 EndZ=0
    g159: LineSegment StartX=16.45 StartY=1.6 StartZ=0 EndX=15.85 EndY=1.6 EndZ=0
  constraints (480):
    c: Coincident(g0,g1)
    c: Coincident(g1,g2)
    c: Coincident(g2,g3)
    c: Coincident(g3,g0)
    c: Vertical(g0)
    c: Vertical(g2)
    c: Horizontal(g1)
    c: Horizontal(g3)
    c: DistanceX(g3,g3) = 0.6
    c: DistanceY(g2,g2) = 0.6
    c: Coincident(g4,g5)
    c: Coincident(g5,g6)
    c: Coincident(g6,g7)
    c: Coincident(g7,g4)
    c: Vertical(g4)
    c: Vertical(g6)
    c: Horizontal(g5)
    c: Horizontal(g7)
    c: DistanceX(g7,g7) = 0.6
    c: DistanceY(g6,g6) = 0.6
    c: Vertical(g4,g0)
    c: Distance(g3,g5) = 1.9
    c: Coincident(g8,g9)
    c: Coincident(g9,g10)
    c: Coincident(g10,g11)
    c: Coincident(g11,g8)
    c: Vertical(g8)
    c: Vertical(g10)
    c: Horizontal(g9)
    c: Horizontal(g11)
    c: DistanceX(g11,g11) = 0.6
    c: DistanceY(g10,g10) = 0.6
    c: Coincident(g12,g13)
    c: Coincident(g13,g14)
    c: Coincident(g14,g15)
    c: Coincident(g15,g12)
    c: Vertical(g12)
    c: Vertical(g14)
    c: Horizontal(g13)
    c: Horizontal(g15)
    c: DistanceX(g15,g15) = 0.6
    c: DistanceY(g14,g14) = 0.6
    c: Vertical(g12,g8)
    c: Distance(g11,g13) = 1.9
    c: Horizontal(g4,g14)
    c: Distance(g14,g4) = 1.9
    c: Coincident(g16,g17)
    c: Coincident(g17,g18)
    c: Coincident(g18,g19)
    c: Coincident(g19,g16)
    c: Vertical(g16)
    c: Vertical(g18)
    c: Horizontal(g17)
    c: Horizontal(g19)
    c: DistanceX(g19,g19) = 0.6
    c: DistanceY(g18,g18) = 0.6
    c: Coincident(g20,g21)
    c: Coincident(g21,g22)
    c: Coincident(g22,g23)
    c: Coincident(g23,g20)
    c: Vertical(g20)
    c: Vertical(g22)
    c: Horizontal(g21)
    c: Horizontal(g23)
    c: DistanceX(g23,g23) = 0.6
    c: DistanceY(g22,g22) = 0.6
    c: Vertical(g20,g16)
    c: Distance(g19,g21) = 1.9
    c: Coincident(g24,g25)
    c: Coincident(g25,g26)
    c: Coincident(g26,g27)
    c: Coincident(g27,g24)
    c: Vertical(g24)
    c: Vertical(g26)
    c: Horizontal(g25)
    c: Horizontal(g27)
    c: DistanceX(g27,g27) = 0.6
    c: DistanceY(g26,g26) = 0.6
    c: Coincident(g28,g29)
    c: Coincident(g29,g30)
    c: Coincident(g30,g31)
    c: Coincident(g31,g28)
    c: Vertical(g28)
    c: Vertical(g30)
    c: Horizontal(g29)
    c: Horizontal(g31)
    c: DistanceX(g31,g31) = 0.6
    c: DistanceY(g30,g30) = 0.6
    c: Vertical(g28,g24)
    c: Distance(g27,g29) = 1.9
    c: Horizontal(g20,g30)
    c: Distance(g30,g20) = 1.9
    c: Horizontal(g8,g17)
    c: Distance(g18,g8) = 1.9
    c: Coincident(g32,g33)
    c: Coincident(g33,g34)
    c: Coincident(g34,g35)
    c: Coincident(g35,g32)
    c: Vertical(g32)
    c: Vertical(g34)
    c: Horizontal(g33)
    c: Horizontal(g35)
    c: DistanceX(g35,g35) = 0.6
    c: DistanceY(g34,g34) = 0.6
    c: Coincident(g36,g37)
    c: Coincident(g37,g38)
    c: Coincident(g38,g39)
    c: Coincident(g39,g36)
    c: Vertical(g36)
    c: Vertical(g38)
    c: Horizontal(g37)
    c: Horizontal(g39)
    c: DistanceX(g39,g39) = 0.6
    c: DistanceY(g38,g38) = 0.6
    c: Vertical(g36,g32)
    c: Distance(g35,g37) = 1.9
    c: Coincident(g40,g41)
    c: Coincident(g41,g42)
    c: Coincident(g42,g43)
    c: Coincident(g43,g40)
    c: Vertical(g40)
    c: Vertical(g42)
    c: Horizontal(g41)
    c: Horizontal(g43)
    c: DistanceX(g43,g43) = 0.6
    c: DistanceY(g42,g42) = 0.6
    c: Coincident(g44,g45)
    c: Coincident(g45,g46)
    c: Coincident(g46,g47)
    c: Coincident(g47,g44)
    c: Vertical(g44)
    c: Vertical(g46)
    c: Horizontal(g45)
    c: Horizontal(g47)
    c: DistanceX(g47,g47) = 0.6
    c: DistanceY(g46,g46) = 0.6
    c: Vertical(g44,g40)
    c: Distance(g43,g45) = 1.9
    c: Horizontal(g36,g46)
    c: Distance(g46,g36) = 1.9
    c: Coincident(g48,g49)
    c: Coincident(g49,g50)
    c: Coincident(g50,g51)
    c: Coincident(g51,g48)
    c: Vertical(g48)
    c: Vertical(g50)
    c: Horizontal(g49)
    c: Horizontal(g51)
    c: DistanceX(g51,g51) = 0.6
    c: DistanceY(g50,g50) = 0.6
    c: Coincident(g52,g53)
    c: Coincident(g53,g54)
    c: Coincident(g54,g55)
    c: Coincident(g55,g52)
    c: Vertical(g52)
    c: Vertical(g54)
    c: Horizontal(g53)
    c: Horizontal(g55)
    c: DistanceX(g55,g55) = 0.6
    c: DistanceY(g54,g54) = 0.6
    c: Vertical(g52,g48)
    c: Distance(g51,g53) = 1.9
    c: Coincident(g56,g57)
    c: Coincident(g57,g58)
    c: Coincident(g58,g59)
    c: Coincident(g59,g56)
    c: Vertical(g56)
    c: Vertical(g58)
    c: Horizontal(g57)
    c: Horizontal(g59)
    c: DistanceX(g59,g59) = 0.6
    c: DistanceY(g58,g58) = 0.6
    c: Coincident(g60,g61)
    c: Coincident(g61,g62)
    c: Coincident(g62,g63)
    c: Coincident(g63,g60)
    c: Vertical(g60)
    c: Vertical(g62)
    c: Horizontal(g61)
    c: Horizontal(g63)
    c: DistanceX(g63,g63) = 0.6
    c: DistanceY(g62,g62) = 0.6
    c: Vertical(g60,g56)
    c: Distance(g59,g61) = 1.9
    c: Horizontal(g52,g62)
    c: Distance(g62,g52) = 1.9
    c: Horizontal(g40,g49)
    c: Distance(g50,g40) = 1.9
    c: Horizontal(g24,g33)
    c: Distance(g24,g34) = 1.9
    c: Coincident(g64,g65)
    c: Coincident(g65,g66)
    c: Coincident(g66,g67)
    c: Coincident(g67,g64)
    c: Vertical(g64)
    c: Vertical(g66)
    c: Horizontal(g65)
    c: Horizontal(g67)
    c: DistanceX(g67,g67) = 0.6
    c: DistanceY(g66,g66) = 0.6
    c: Coincident(g68,g69)
    c: Coincident(g69,g70)
    c: Coincident(g70,g71)
    c: Coincident(g71,g68)
    c: Vertical(g68)
    c: Vertical(g70)
    c: Horizontal(g69)
    c: Horizontal(g71)
    c: DistanceX(g71,g71) = 0.6
    c: DistanceY(g70,g70) = 0.6
    c: Vertical(g68,g64)
    c: Distance(g67,g69) = 1.9
    c: Coincident(g72,g73)
    c: Coincident(g73,g74)
    c: Coincident(g74,g75)
    c: Coincident(g75,g72)
    c: Vertical(g72)
    c: Vertical(g74)
    c: Horizontal(g73)
    c: Horizontal(g75)
    c: DistanceX(g75,g75) = 0.6
    c: DistanceY(g74,g74) = 0.6
    c: Coincident(g76,g77)
    c: Coincident(g77,g78)
    c: Coincident(g78,g79)
    c: Coincident(g79,g76)
    c: Vertical(g76)
    c: Vertical(g78)
    c: Horizontal(g77)
    c: Horizontal(g79)
    c: DistanceX(g79,g79) = 0.6
    c: DistanceY(g78,g78) = 0.6
    c: Vertical(g76,g72)
    c: Distance(g75,g77) = 1.9
    c: Horizontal(g68,g78)
    c: Distance(g78,g68) = 1.9
    c: Coincident(g80,g81)
    c: Coincident(g81,g82)
    c: Coincident(g82,g83)
    c: Coincident(g83,g80)
    c: Vertical(g80)
    c: Vertical(g82)
    c: Horizontal(g81)
    c: Horizontal(g83)
    c: DistanceX(g83,g83) = 0.6
    c: DistanceY(g82,g82) = 0.6
    c: Coincident(g84,g85)
    c: Coincident(g85,g86)
    c: Coincident(g86,g87)
    c: Coincident(g87,g84)
    c: Vertical(g84)
    c: Vertical(g86)
    c: Horizontal(g85)
    c: Horizontal(g87)
    c: DistanceX(g87,g87) = 0.6
    c: DistanceY(g86,g86) = 0.6
    c: Vertical(g84,g80)
    c: Distance(g83,g85) = 1.9
    c: Coincident(g88,g89)
    c: Coincident(g89,g90)
    c: Coincident(g90,g91)
    c: Coincident(g91,g88)
    c: Vertical(g88)
    c: Vertical(g90)
    c: Horizontal(g89)
    c: Horizontal(g91)
    c: DistanceX(g91,g91) = 0.6
    c: DistanceY(g90,g90) = 0.6
    c: Coincident(g92,g93)
    c: Coincident(g93,g94)
    c: Coincident(g94,g95)
    c: Coincident(g95,g92)
    c: Vertical(g92)
    c: Vertical(g94)
    c: Horizontal(g93)
    c: Horizontal(g95)
    c: DistanceX(g95,g95) = 0.6
    c: DistanceY(g94,g94) = 0.6
    c: Vertical(g92,g88)
    c: Distance(g91,g93) = 1.9
    c: Horizontal(g84,g94)
    c: Distance(g94,g84) = 1.9
    c: Horizontal(g72,g81)
    c: Distance(g82,g72) = 1.9
    c: Coincident(g96,g97)
    c: Coincident(g97,g98)
    c: Coincident(g98,g99)
    c: Coincident(g99,g96)
    c: Vertical(g96)
    c: Vertical(g98)
    c: Horizontal(g97)
    c: Horizontal(g99)
    c: DistanceX(g99,g99) = 0.6
    c: DistanceY(g98,g98) = 0.6
    c: Coincident(g100,g101)
    c: Coincident(g101,g102)
    c: Coincident(g102,g103)
    c: Coincident(g103,g100)
    c: Vertical(g100)
    c: Vertical(g102)
    c: Horizontal(g101)
    c: Horizontal(g103)
    c: DistanceX(g103,g103) = 0.6
    c: DistanceY(g102,g102) = 0.6
    c: Vertical(g100,g96)
    c: Distance(g99,g101) = 1.9
    c: Coincident(g104,g105)
    c: Coincident(g105,g106)
    c: Coincident(g106,g107)
    c: Coincident(g107,g104)
    c: Vertical(g104)
    c: Vertical(g106)
    c: Horizontal(g105)
    c: Horizontal(g107)
    c: DistanceX(g107,g107) = 0.6
    c: DistanceY(g106,g106) = 0.6
    c: Coincident(g108,g109)
    c: Coincident(g109,g110)
    c: Coincident(g110,g111)
    c: Coincident(g111,g108)
    c: Vertical(g108)
    c: Vertical(g110)
    c: Horizontal(g109)
    c: Horizontal(g111)
    c: DistanceX(g111,g111) = 0.6
    c: DistanceY(g110,g110) = 0.6
    c: Vertical(g108,g104)
    c: Distance(g107,g109) = 1.9
    c: Horizontal(g100,g110)
    c: Distance(g110,g100) = 1.9
    c: Coincident(g112,g113)
    c: Coincident(g113,g114)
    c: Coincident(g114,g115)
    c: Coincident(g115,g112)
    c: Vertical(g112)
    c: Vertical(g114)
    c: Horizontal(g113)
    c: Horizontal(g115)
    c: DistanceX(g115,g115) = 0.6
    c: DistanceY(g114,g114) = 0.6
    c: Coincident(g116,g117)
    c: Coincident(g117,g118)
    c: Coincident(g118,g119)
    c: Coincident(g119,g116)
    c: Vertical(g116)
    c: Vertical(g118)
    c: Horizontal(g117)
    c: Horizontal(g119)
    c: DistanceX(g119,g119) = 0.6
    c: DistanceY(g118,g118) = 0.6
    c: Vertical(g116,g112)
    c: Distance(g115,g117) = 1.9
    c: Coincident(g120,g121)
    c: Coincident(g121,g122)
    c: Coincident(g122,g123)
    c: Coincident(g123,g120)
    c: Vertical(g120)
    c: Vertical(g122)
    c: Horizontal(g121)
    c: Horizontal(g123)
    c: DistanceX(g123,g123) = 0.6
    c: DistanceY(g122,g122) = 0.6
    c: Coincident(g124,g125)
    c: Coincident(g125,g126)
    c: Coincident(g126,g127)
    c: Coincident(g127,g124)
    c: Vertical(g124)
    c: Vertical(g126)
    c: Horizontal(g125)
    c: Horizontal(g127)
    c: DistanceX(g127,g127) = 0.6
    c: DistanceY(g126,g126) = 0.6
    c: Vertical(g124,g120)
    c: Distance(g123,g125) = 1.9
    c: Horizontal(g116,g126)
    c: Distance(g126,g116) = 1.9
    c: Horizontal(g104,g113)
    c: Distance(g114,g104) = 1.9
    c: Horizontal(g88,g97)
    c: Distance(g88,g98) = 1.9
    c: Horizontal(g65,g56)
    c: Distance(g56,g66) = 1.9
    c: Coincident(g128,g129)
    c: Coincident(g129,g130)
    c: Coincident(g130,g131)
    c: Coincident(g131,g128)
    c: Vertical(g128)
    c: Vertical(g130)
    c: Horizontal(g129)
    c: Horizontal(g131)
    c: DistanceX(g131,g131) = 0.6
    c: DistanceY(g130,g130) = 0.6
    c: Coincident(g132,g133)
    c: Coincident(g133,g134)
    c: Coincident(g134,g135)
    c: Coincident(g135,g132)
    c: Vertical(g132)
    c: Vertical(g134)
    c: Horizontal(g133)
    c: Horizontal(g135)
    c: DistanceX(g135,g135) = 0.6
    c: DistanceY(g134,g134) = 0.6
    c: Vertical(g132,g128)
    c: Distance(g131,g133) = 1.9
    c: Coincident(g136,g137)
    c: Coincident(g137,g138)
    c: Coincident(g138,g139)
    c: Coincident(g139,g136)
    c: Vertical(g136)
    c: Vertical(g138)
    c: Horizontal(g137)
    c: Horizontal(g139)
    c: DistanceX(g139,g139) = 0.6
    c: DistanceY(g138,g138) = 0.6
    c: Coincident(g140,g141)
    c: Coincident(g141,g142)
    c: Coincident(g142,g143)
    c: Coincident(g143,g140)
    c: Vertical(g140)
    c: Vertical(g142)
    c: Horizontal(g141)
    c: Horizontal(g143)
    c: DistanceX(g143,g143) = 0.6
    c: DistanceY(g142,g142) = 0.6
    c: Vertical(g140,g136)
    c: Distance(g139,g141) = 1.9
    c: Horizontal(g132,g142)
    c: Distance(g142,g132) = 1.9
    c: Coincident(g144,g145)
    c: Coincident(g145,g146)
    c: Coincident(g146,g147)
    c: Coincident(g147,g144)
    c: Vertical(g144)
    c: Vertical(g146)
    c: Horizontal(g145)
    c: Horizontal(g147)
    c: DistanceX(g147,g147) = 0.6
    c: DistanceY(g146,g146) = 0.6
    c: Coincident(g148,g149)
    c: Coincident(g149,g150)
    c: Coincident(g150,g151)
    c: Coincident(g151,g148)
    c: Vertical(g148)
    c: Vertical(g150)
    c: Horizontal(g149)
    c: Horizontal(g151)
    c: DistanceX(g151,g151) = 0.6
    c: DistanceY(g150,g150) = 0.6
    c: Vertical(g148,g144)
    c: Distance(g147,g149) = 1.9
    c: Coincident(g152,g153)
    c: Coincident(g153,g154)
    c: Coincident(g154,g155)
    c: Coincident(g155,g152)
    c: Vertical(g152)
    c: Vertical(g154)
    c: Horizontal(g153)
    c: Horizontal(g155)
    c: DistanceX(g155,g155) = 0.6
    c: DistanceY(g154,g154) = 0.6
    c: Coincident(g156,g157)
    c: Coincident(g157,g158)
    c: Coincident(g158,g159)
    c: Coincident(g159,g156)
    c: Vertical(g156)
    c: Vertical(g158)
    c: Horizontal(g157)
    c: Horizontal(g159)
    c: DistanceX(g159,g159) = 0.6
    c: DistanceY(g158,g158) = 0.6
    c: Vertical(g156,g152)
    c: Distance(g155,g157) = 1.9
    c: Horizontal(g148,g158)
    c: Distance(g158,g148) = 1.9
    c: Horizontal(g136,g145)
    c: Distance(g146,g136) = 1.9
    c: Horizontal(g1,g152)
    c: Distance(g152,g2) = 1.9
    c: Distance(g-4,g120) = 1.5
    c: Distance(g-5,g121) = 1
FEATURE [PartDesign::Pocket] Pocket002
  BaseFeature = -> Pad009
  Direction = (0,0,-1)
  Length = 5
  Length2 = 5
  Profile = -> Sketch013
  ReferenceAxis = -> Sketch013 [N_Axis]
  Refine = true
  Suppressed = false
  Type = 0
FEATURE [PartDesign::Body] Body007  label="Pin Block"
  AllowCompound = false
  Group = -> [Sketch012,Pad009,Sketch013,Pocket002]
  Origin = -> Origin013
  Tip = -> Pocket002
PROVENANCE & LICENSES
A FreeCAD (.FCStd) document from a public repository crawl; recipes are the document's own serialized feature recipes (and, for linked parts, companion documents' recipes).
License: as declared in the source repository (recorded in the dataset sidecar).
